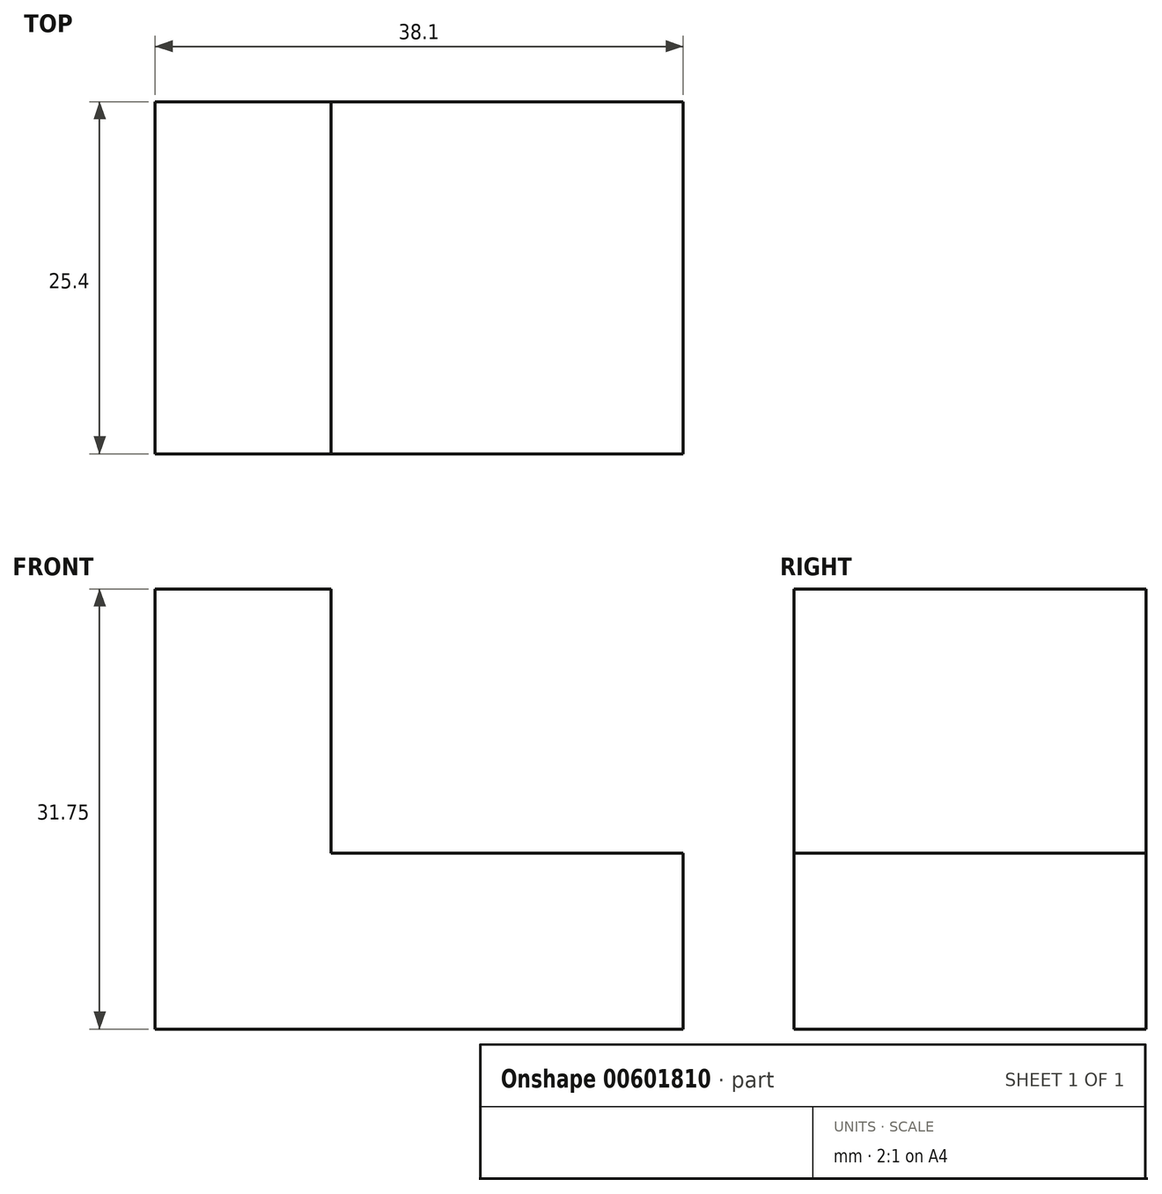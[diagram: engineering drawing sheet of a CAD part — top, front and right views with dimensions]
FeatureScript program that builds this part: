
annotation { "Feature Type Name" : "Feature", "Feature Type Description" : "" }
export const myFeature = defineFeature(function(context is Context, id is Id, definition is map)
    precondition{}
    {
        {
            var Q0;
            Q0=qCreatedBy(makeId("Front.planeOp"),FACE);
            var sketch = newSketch(context, id + "F0", { "sketchPlane" : qUnion([Q0])});
            skLineSegment(sketch, "E0", {"start": v(0, 0) * mm, "end": v(0, 31.75) * mm});
            skLineSegment(sketch, "E1", {"start": v(12.7, 31.75) * mm, "end": v(0, 31.75) * mm});
            skLineSegment(sketch, "E2", {"start": v(12.7, 31.75) * mm, "end": v(12.7, 12.7) * mm});
            skLineSegment(sketch, "E3", {"start": v(12.7, 12.7) * mm, "end": v(38.1, 12.7) * mm});
            skLineSegment(sketch, "E4", {"start": v(38.1, 12.7) * mm, "end": v(38.1, 0) * mm});
            skLineSegment(sketch, "E5", {"start": v(38.1, 0) * mm, "end": v(0, 0) * mm});
            skSolve(sketch);
        }
        {
            var Q0;
            Q0=makeQuery(id+"F0.imprint","IMPRINT",FACE,{"disambiguationData":[TD([[makeQuery(id+"F0.imprint","IMPRINT",EDGE,{"derivedFrom":sQuery(id+"F0.wireOp",EDGE,"E0")}),-1.0]])]});
            extrude(context, id + "F1", {"entities" : qUnion([Q0]), "depth" : 25.4 * mm, "offsetDistance" : 25.4 * mm});
        }
    });
